# Revit family: SYSCOOL FLOOR 60 HP R, наружный  блок
name_source: partatom
category: Оборудование
units: mm (PartAtom-declared; Revit-internal decimal feet)

## family parameters
Всегда вертикально = Да
Заголовок OmniClass = Climate Control (HVAC)
На основе рабочей плоскости = Нет
Номер OmniClass = 23.75.00.00
Общий = Нет
При загрузке вырезать с полостями = Нет
Размер круглого соединителя = Использовать диаметр
Тип детали = Нормальный
Точка расчета площади = Нет

## types (1)
- MODU-55HN1-R
    Air Flow = 3800.00 м³/ч
    Casing color = SB2098
    Compressor = 1
    Cooling Power Input = 0.00 кВт
    Depth = 410 мм
    Gas = R410A
    Gas pipe = 15.9 мм
    Gas pipe Radius = 7.95 мм
    Heating Power Input = 0.00 кВт
    Height = 810 мм
    Installation = Outdoor installation
    Liquid pipe = 9.52 мм
    Liquid pipe Radius = 4.76 мм
    Maximum Fuse Amps = 25 А
    Min cable selection (power wiring) = 5x2.5
    Minimum Circuit Amps = 13 А
    Net Weight = 99.70 кг
    Power supply = 380-415V,3Ph,50Hz
    Width = 946 мм
    clearance access behind = 300 мм
    clearance access front = 2000 мм
    clearance access left = 300 мм
    clearance access right = 600 мм
    Группа модели = MODU-55HN1-R

## geometry (parser evidence)
native form markers: Sweep x19
no freeform markers — native parametric forms only
